# Revit family: Steel-HST Top Hat-Steel & Tube-G500A
name_source: partatom
category: Structural Framing
revit_build: Autodesk Revit 2016 (Build: 20160314_0715(x64)
units: mm (PartAtom-declared; Revit-internal decimal feet)

## family parameters
Always export as geometry = No
Always vertical = Yes
Cut with Voids When Loaded = No
Material for Model Behavior = Steel
OmniClass Number = 23.25.30.11.14.14
OmniClass Title = Beams
Section Shape = User Defined
Shared = No
Show family pre-cut in plan views = Yes
Structural Framing Length Roundoff = 0 mm

## types (1)
- 60 HST Tophat 0.75 BMT
    Assembly Code = B1020230
    CBICode = 3411
    CBIDescription = Structural steelwork
    Centroid Horizontal = 54.3 mm
    Centroid Vertical = 31.7 mm
    Coil Performance = Gauge 0.75-1.15mm; G500(MPa); 275g/m² (Zinc)
    Description = Steel & Tube HST Tophat sections are an economical, lightweight, versatile and easy to use product for roof purlins, wall girts and floor joists.
    Design Instruction = All the design information should be cross referenced with the current Steel & Tube Tophat Design Capacity Tables.
    Design Standard = Steel & Tube’s HST Tophat profiles are designed in accordance with AS/NZS 4600:2005
    Elastic Modulus strong axis = 2450.0 mm³
    Elastic Modulus weak axis = 2200.0 mm³
    Flange Thickness = 0.8 mm
    Height = 60.0 mm
    Manufacturer = Steel & Tube
    ManufacturerName = Steel & Tube
    ManufacturerURL = http://www.steelandtube.co.nz
    MassPerUnitLength_ANZRS = 1.18 kg/m
    Material Standard = Steel & Tube’s HST Tophat profiles are manufactured from materials conforming to AS1397:2011
    Model = 60 HST Tophat 0.75 BMT
    ModifiedIssue_ANZRS = 20160401.01 $
    Moment of Inertia strong axis = 78000.00 mm4
    Moment of Inertia weak axis = 119000.00 mm4
    Nominal Weight = 1.18 kgf/m
    Perimeter = 0.00 m²/m
    Plastic Modulus strong axis = 2450.0 mm³
    Plastic Modulus weak axis = 2200.0 mm³
    Principal Axes Angle = 90.00°
    Profile1 = Yes
    Profile2 = No
    Profile2 Size = 3
    Section Area = 150.0 mm²
    SectionAreaGross_ANZRS = 150.0 mm²
    SectionAreaNet_ANZRS = 150.0 mm²
    Shear Area strong axis = 150.0 mm²
    Shear Area weak axis = 150.0 mm²
    SpecificationDescription = Steel & Tube Purlins & Girts
    SpecificationReference = 3411ST
    StickSymbolEndCutBack_ANZRS = 100 mm  [stored 0.328084 ft]
    Structural Material = Metal-Steel-500MPa
    Torsional Modulus = 0.0 mm³
    Torsional Moment of Inertia = 28.20 mm4
    URL = http://www.steelandtube.co.nz
    Uniclass2015Code = Pr_20_76_51_21
    Uniclass2015Title = Cold-formed galvanized steel sections
    Uniclass2015Version = 2015
    Warping Constant = 16050000000.0 mm6
    Width = 108.5 mm

note: [stored X ft] marks values corroborated as IEEE doubles in the binary element streams (Revit-internal decimal feet)

## geometry (parser evidence)
native form markers: Sweep x5
no freeform markers — native parametric forms only
